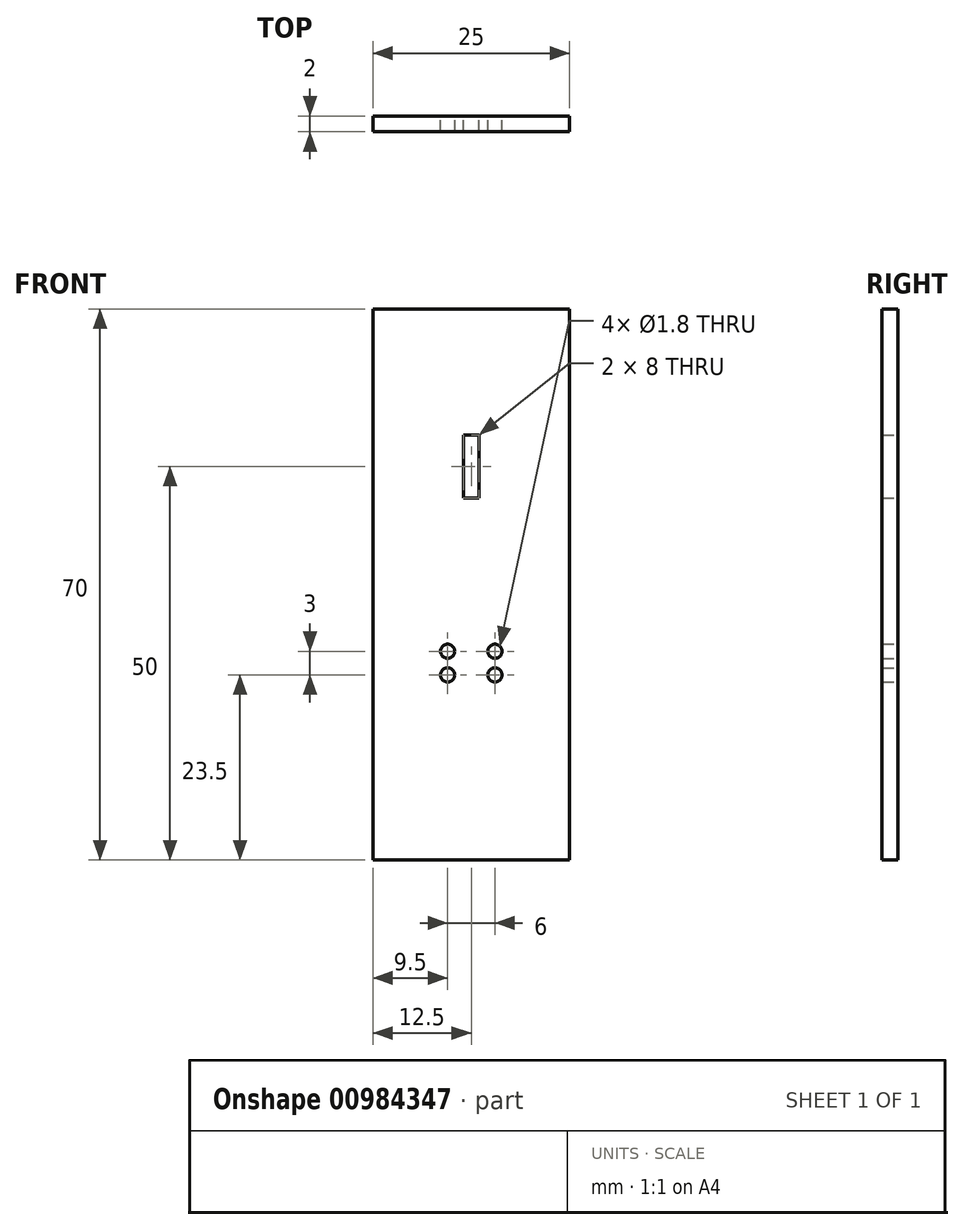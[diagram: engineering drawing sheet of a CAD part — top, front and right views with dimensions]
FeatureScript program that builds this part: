
annotation { "Feature Type Name" : "Feature", "Feature Type Description" : "" }
export const myFeature = defineFeature(function(context is Context, id is Id, definition is map)
    precondition{}
    {
        {
            var Q0;
            Q0=qCreatedBy(makeId("Front.planeOp"),FACE);
            var sketch = newSketch(context, id + "F0", { "sketchPlane" : qUnion([Q0])});
            skLineSegment(sketch, "E0.bottom", {"start": v(12.5, -35) * mm, "end": v(-12.5, -35) * mm});
            skLineSegment(sketch, "E0.top", {"start": v(12.5, 35) * mm, "end": v(-12.5, 35) * mm});
            skLineSegment(sketch, "E0.left", {"start": v(12.5, -35) * mm, "end": v(12.5, 35) * mm});
            skLineSegment(sketch, "E0.right", {"start": v(-12.5, -35) * mm, "end": v(-12.5, 35) * mm});
            skPoint(sketch, "E0.middle", {"position": v(0, 0) * mm});
            skLineSegment(sketch, "E1.bottom", {"start": v(1, 11) * mm, "end": v(-1, 11) * mm});
            skLineSegment(sketch, "E1.top", {"start": v(1, 19) * mm, "end": v(-1, 19) * mm});
            skLineSegment(sketch, "E1.left", {"start": v(1, 11) * mm, "end": v(1, 19) * mm});
            skLineSegment(sketch, "E1.right", {"start": v(-1, 11) * mm, "end": v(-1, 19) * mm});
            skPoint(sketch, "E1.middle", {"position": v(0, 15) * mm});
            skLineSegment(sketch, "E2.bottom", {"start": v(3, -11.5) * mm, "end": v(-3, -11.5) * mm, "construction": true});
            skLineSegment(sketch, "E2.top", {"start": v(3, -8.5) * mm, "end": v(-3, -8.5) * mm, "construction": true});
            skLineSegment(sketch, "E2.left", {"start": v(3, -11.5) * mm, "end": v(3, -8.5) * mm, "construction": true});
            skLineSegment(sketch, "E2.right", {"start": v(-3, -11.5) * mm, "end": v(-3, -8.5) * mm, "construction": true});
            skPoint(sketch, "E2.middle", {"position": v(0, -10) * mm});
            skCircle(sketch, "E3", {"center": v(-3, -8.5) * mm, "radius": 0.9 * mm});
            skCircle(sketch, "E4", {"center": v(3, -8.5) * mm, "radius": 0.9 * mm});
            skCircle(sketch, "E5", {"center": v(3, -11.5) * mm, "radius": 0.9 * mm});
            skCircle(sketch, "E6", {"center": v(-3, -11.5) * mm, "radius": 0.9 * mm});
            skSolve(sketch);
        }
        {
            var Q0;
            Q0=makeQuery(id+"F0.imprint","IMPRINT",FACE,{"disambiguationData":[TD([[makeQuery(id+"F0.imprint","IMPRINT",EDGE,{"derivedFrom":sQuery(id+"F0.wireOp",EDGE,"E0.bottom")}),-1.0]])]});
            extrude(context, id + "F1", {"entities" : qUnion([Q0]), "depth" : 2 * mm, "offsetDistance" : 25 * mm});
        }
    });
